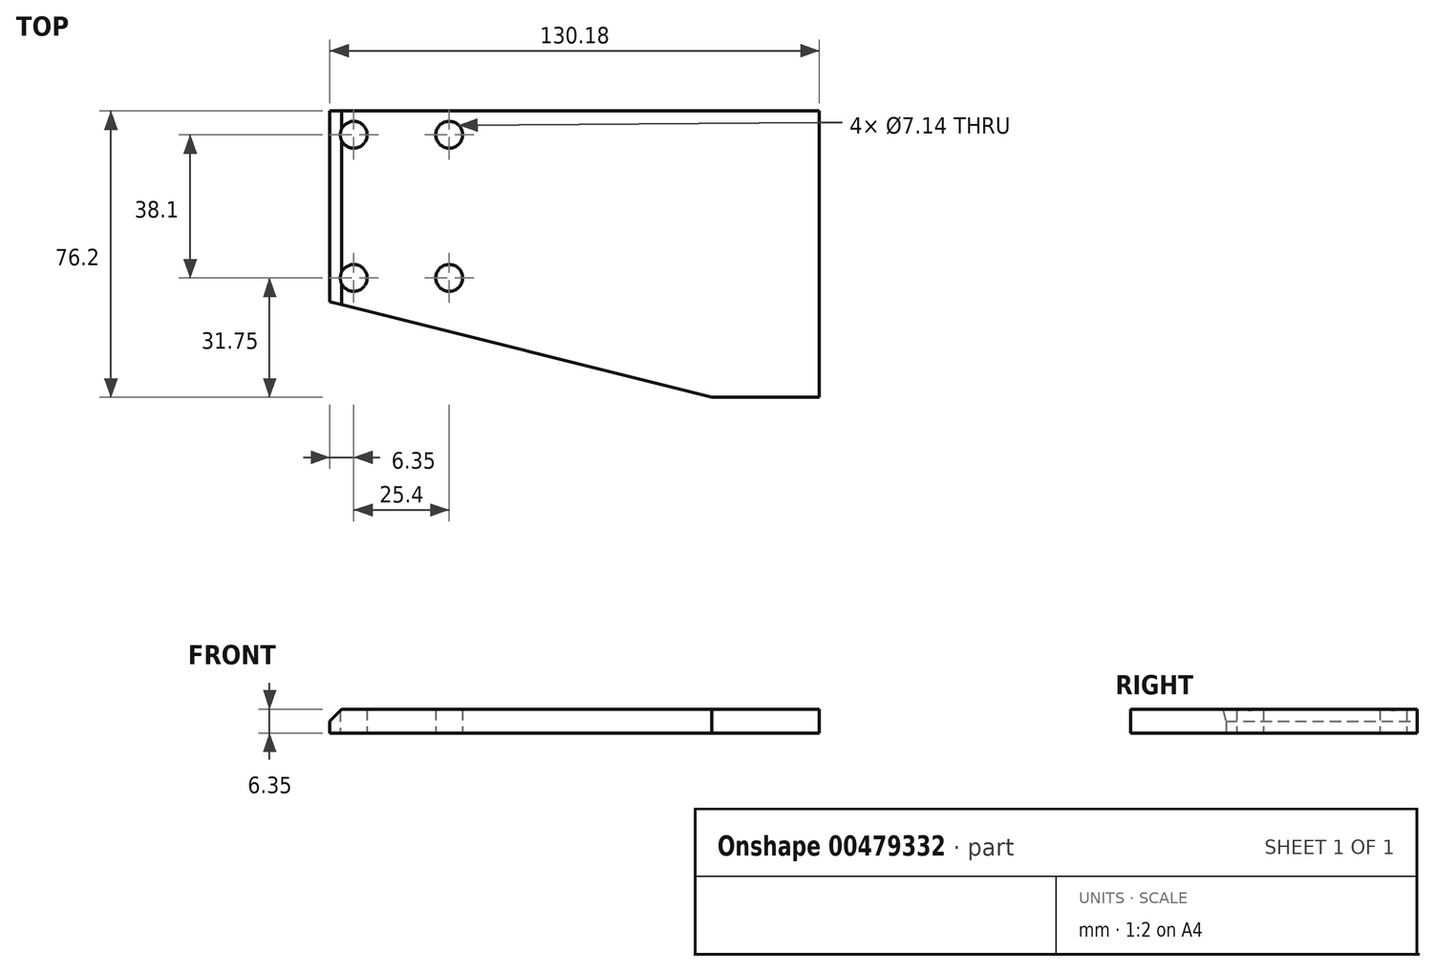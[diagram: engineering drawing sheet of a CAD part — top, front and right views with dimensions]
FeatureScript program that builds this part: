
annotation { "Feature Type Name" : "Feature", "Feature Type Description" : "" }
export const myFeature = defineFeature(function(context is Context, id is Id, definition is map)
    precondition{}
    {
        {
            var Q0;
            Q0=qCreatedBy(makeId("Top.planeOp"),FACE);
            var sketch = newSketch(context, id + "F0", { "sketchPlane" : qUnion([Q0])});
            skLineSegment(sketch, "E0.bottom", {"start": v(0, 0) * mm, "end": v(130.18, 0) * mm});
            skLineSegment(sketch, "E0.right", {"start": v(130.18, 0) * mm, "end": v(130.18, -76.2) * mm});
            skLineSegment(sketch, "E1", {"start": v(0, 0) * mm, "end": v(0, -50.8) * mm});
            skLineSegment(sketch, "E2", {"start": v(101.6, -76.2) * mm, "end": v(0, -50.8) * mm});
            skLineSegment(sketch, "E3", {"start": v(101.6, -76.2) * mm, "end": v(130.18, -76.2) * mm});
            skCircle(sketch, "E4", {"center": v(6.35, -6.35) * mm, "radius": 3.57 * mm});
            skCircle(sketch, "E5.0.1.0", {"center": v(6.35, -44.45) * mm, "radius": 3.57 * mm});
            skCircle(sketch, "E5.1.0.0", {"center": v(31.75, -6.35) * mm, "radius": 3.57 * mm});
            skCircle(sketch, "E5.1.1.0", {"center": v(31.75, -44.45) * mm, "radius": 3.57 * mm});
            skLineSegment(sketch, "E5.direction1", {"start": v(6.35, -6.35) * mm, "end": v(31.75, -6.35) * mm, "construction": true});
            skLineSegment(sketch, "E5.direction2", {"start": v(6.35, -6.35) * mm, "end": v(6.35, -44.45) * mm, "construction": true});
            skSolve(sketch);
        }
        {
            var Q0;
            Q0=makeQuery(id+"F0.imprint","IMPRINT",FACE,{"disambiguationData":[TD([[makeQuery(id+"F0.imprint","IMPRINT",EDGE,{"derivedFrom":sQuery(id+"F0.wireOp",EDGE,"E0.bottom")}),-1.0]])]});
            extrude(context, id + "F1", {"entities" : qUnion([Q0]), "depth" : 6.35 * mm});
        }
        {
            var Q0;
            Q0=makeQuery(id+"F1.opExtrude","CAP_EDGE",EDGE,{"disambiguationData":[OSD([sQuery(id+"F0.wireOp",EDGE,"E1")])],"isStart":false});
            chamfer(context, id + "F2", {"entities" : qUnion([Q0]), "width" : 3.17 * mm, "tangentPropagation" : true});
        }
    });
